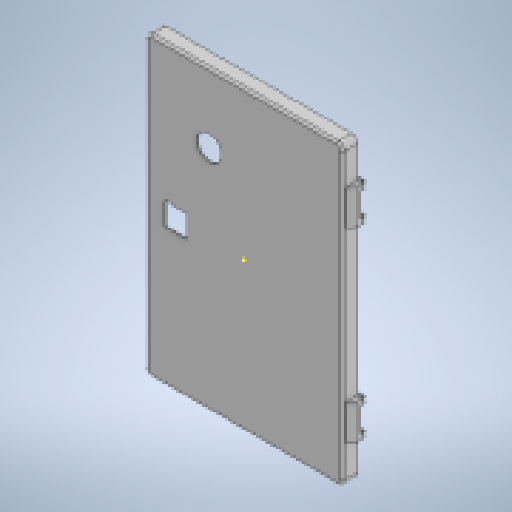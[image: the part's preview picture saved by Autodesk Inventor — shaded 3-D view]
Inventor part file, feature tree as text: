
AUTODESK INVENTOR PART (.ipt)
format: ipt  version: 2025.2 (Build 292293000, 293)  size: 430,080 bytes
history: native  units: mm
features: other x28, sketch x23, extrude x12, revolve x9, thread x1
ambient origin geometry x8: Origin, YZ Plane, XZ Plane, XY Plane, X Axis, Y Axis, Z Axis, Center Point
bodies: Solid1 (feature_tree)
feature tree (73):
  extrude  "Extrusion1"  Depth=286.0mm TaperAngle=0.0deg
  extrude  "Extrusion2"  TaperAngle=90.0deg  [1 undecoded]
  revolve  "Revolution1"  Angle=90.0deg
  revolve  "Revolution2"  Angle=90.0deg
  revolve  "Revolution3"  Angle=90.0deg
  revolve  "Revolution4"  [1 undecoded]
  extrude  "Extrusion3"  Depth=188.0mm TaperAngle=0.0deg
  revolve  "Revolution5"  Angle=360.0deg
  revolve  "Revolution6"  [1 undecoded]
  revolve  "Revolution7"  [1 undecoded]
  revolve  "Revolution8"  [1 undecoded]
  extrude  "Extrusion4"  Depth=80.0mm
  extrude  "Extrusion5"  Depth=25.0mm
  extrude  "Extrusion6"  Depth=25.0mm
  extrude  "Extrusion7"  Depth=35.0mm
  revolve  "Revolution9"  [1 undecoded]
  thread  "Thread1"  [1 undecoded]
  extrude  "Extrusion8"  [1 undecoded]
  extrude  "Extrusion9"  [1 undecoded]
  extrude  "Extrusion10"  [1 undecoded]
  extrude  "Extrusion11"  [1 undecoded]
  other  "DECKEL_XY"
  other  "DECKEL_YZ"
  other  "DECKEL_ZX"
  other  "DECKEL_X"
  other  "DECKEL_Y"
  other  "DECKEL_Z"
  other  "DECKEL_Center"
  other  "VB_XY"
  other  "VB_YZ"
  other  "VB_ZX"
  other  "VB_X"
  other  "VB_Y"
  other  "VB_Z"
  other  "VB_Center"
  other  "to_HINGE_XY"
  other  "to_HINGE_YZ"
  other  "to_HINGE_ZX"
  other  "to_HINGE_X"
  other  "to_HINGE_Y"
  other  "to_HINGE_Z"
  other  "to_HINGE_Center"
  other  "to_HINGE_1_XY"
  other  "to_HINGE_1_YZ"
  other  "to_HINGE_1_ZX"
  other  "to_HINGE_1_X"
  other  "to_HINGE_1_Y"
  other  "to_HINGE_1_Z"
  other  "to_HINGE_1_Center"
  extrude  "Extrusion12"  [1 undecoded]
  sketch  "Sketch25"
  sketch  "Sketch26"
  sketch  "Skizze_2"  dims[d4=90.0deg d5=90.0deg]
  sketch  "Skizze_4"  dims[d8=176.5mm d9=0.0mm d10=90.0deg]
  sketch  "Skizze_5"  dims[d13=90.0deg d14=276.5mm d15=0.0mm]
  sketch  "Skizze_6"  dims[d20=1.25mm d21=0.0mm d22=360.0deg]
  sketch  "Skizze_7"  dims[d27=35.0mm d28=0.0mm d29=25.0mm d30=0.0mm]
  sketch  "Skizze_8"  dims[d31=25.0mm d32=0.0mm d33=0.0mm]
  sketch  "Skizze_29"
  sketch  "Skizze_30"
  sketch  "Skizze_31"
  sketch  "Skizze_32"
  sketch  "Skizze_33"
  sketch  "Skizze_34"
  sketch  "Sketch_5"  dims[d16=288.0mm d17=0.0mm d18=188.0mm d19=0.0mm]
  sketch  "Sketch_6"  dims[d23=7.1865mm d24=0.0mm d25=35.0mm d26=0.0mm]
  sketch  "Sketch_3"  dims[d6=90.0deg d7=90.0deg]
  sketch  "Sketch_1"  dims[d0=186.0mm d1=0.0mm d2=286.0mm d3=0.0mm]
  sketch  "Sketch_4"  dims[d11=90.0deg d12=90.0deg]
  sketch  "Sketch_10"  dims[d36=35.0mm d37=25.0mm]
  sketch  "Sketch_9"  dims[d34=0.0mm d35=80.0mm]
  sketch  "Sketch_11"  dims[d38=10.0mm d39=0.0mm d41=25.0mm]
  sketch  "Sketch21"  dims[d42=80.0mm d43=35.0mm]
note: 12 required parameter values undecoded (feature->parameter linkage not recoverable at this tier; creation-order binding heuristic only, values carry confidence <= 0.55)